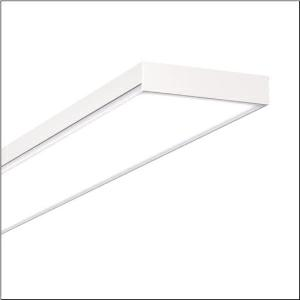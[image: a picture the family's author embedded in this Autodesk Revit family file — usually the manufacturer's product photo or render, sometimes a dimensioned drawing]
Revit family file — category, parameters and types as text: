
# Revit family: apollon_r__31_surface_51mp25wm2441w_5717
name_source: partatom
category: Lighting Fixtures
units: mm (PartAtom-declared; Revit-internal decimal feet)

## family parameters
Cut with Voids When Loaded = No
Host = Face
Light Source = No
Part Type = Normal
Room Calculation Point = No
Round Connector Dimension = Use Diameter
Shared = No

## types (1)
- Apollon® 31 Surface (1 x LED, 3800 lm, 27 W, 4000K)
    Apparent Load = 27 VA
    CIE Flux Codes = 61 87 97 97 100
    Color Rendering = 80
    Color Temperature = 4000K
    Default Elevation = 1800 mm
    Description = Apollon® 31 Surface, office luminaire, primary optical cover: micro prismatic cover, of PMMA, light emission: direct distribution, primary light characteristic: symmetric, installation type: surface-mounted, LED, rated luminous flux: 3.800lm, luminous efficacy: 139lm/W, light colour: 840, colour temperature: 4000K, control gear: ECG Multilumen, with terminal, 3-pole, mains connection: 220..240V, AC, 50/60Hz, rated input power: 27W, housing, of sheet steel, coil coated, traffic white (RAL 9016), length: 1.245mm, width: 200mm, height: 44mm, protection rating (complete): IP20, insulation class (complete): insulation class II (safety insulation), certification: CE, impact resistance: IK02, permissible operating ambient temperature: -20..+40°C, packaging unit: 1 piece
    Height = 44 mm
    Lamp = 1 x LED
    Lamp Light Flux = 3800 lm
    Lamp Power = 27 W
    Lamp count = 1
    Length = 1245 mm
    Luminous efficacy = 141 lm/W
    Manufacturer = Siteco
    ModVariant = No
    Model = 51MP25WM2441W
    Mounting Place = Ceiling
    Mounting Type = Surface mounted
    Number of Poles = 1
    OnlyDefault = Yes
    Power Factor = 1
    Product Name = Apollon® 31 Surface
    Product group = office luminaire | ceiling mounted
    ProductGroupID = 304
    Protection Class = Protection class II
    Protection Degree = IP 20
    RLX_Detail_Level = 1
    RLX_Emergency_Light_Flux = 0 lm
    RLX_Emergency_Type = 0
    RLX_Emergency_Type_DB = No
    RlxData = <blob elided: 20741 chars, md5=eecab0ae>
    Socket = socket
    Standby Power = 0 W
    System Light Flux = 3800 lm
    System Power = 27 W
    Type Comments = Product without accessories
    Type Image = l_1007095.jpg
    URL = http://relux.com
    VarID = ---
    Voltage = 0 V
    Weight = 0.00 kg
    Width = 200 mm  [stored 0.656168 ft]

note: [stored X ft] marks values corroborated as IEEE doubles in the binary element streams (Revit-internal decimal feet)

## geometry (parser evidence)
native form markers: Blend x4, Sweep x10
no freeform markers — native parametric forms only
